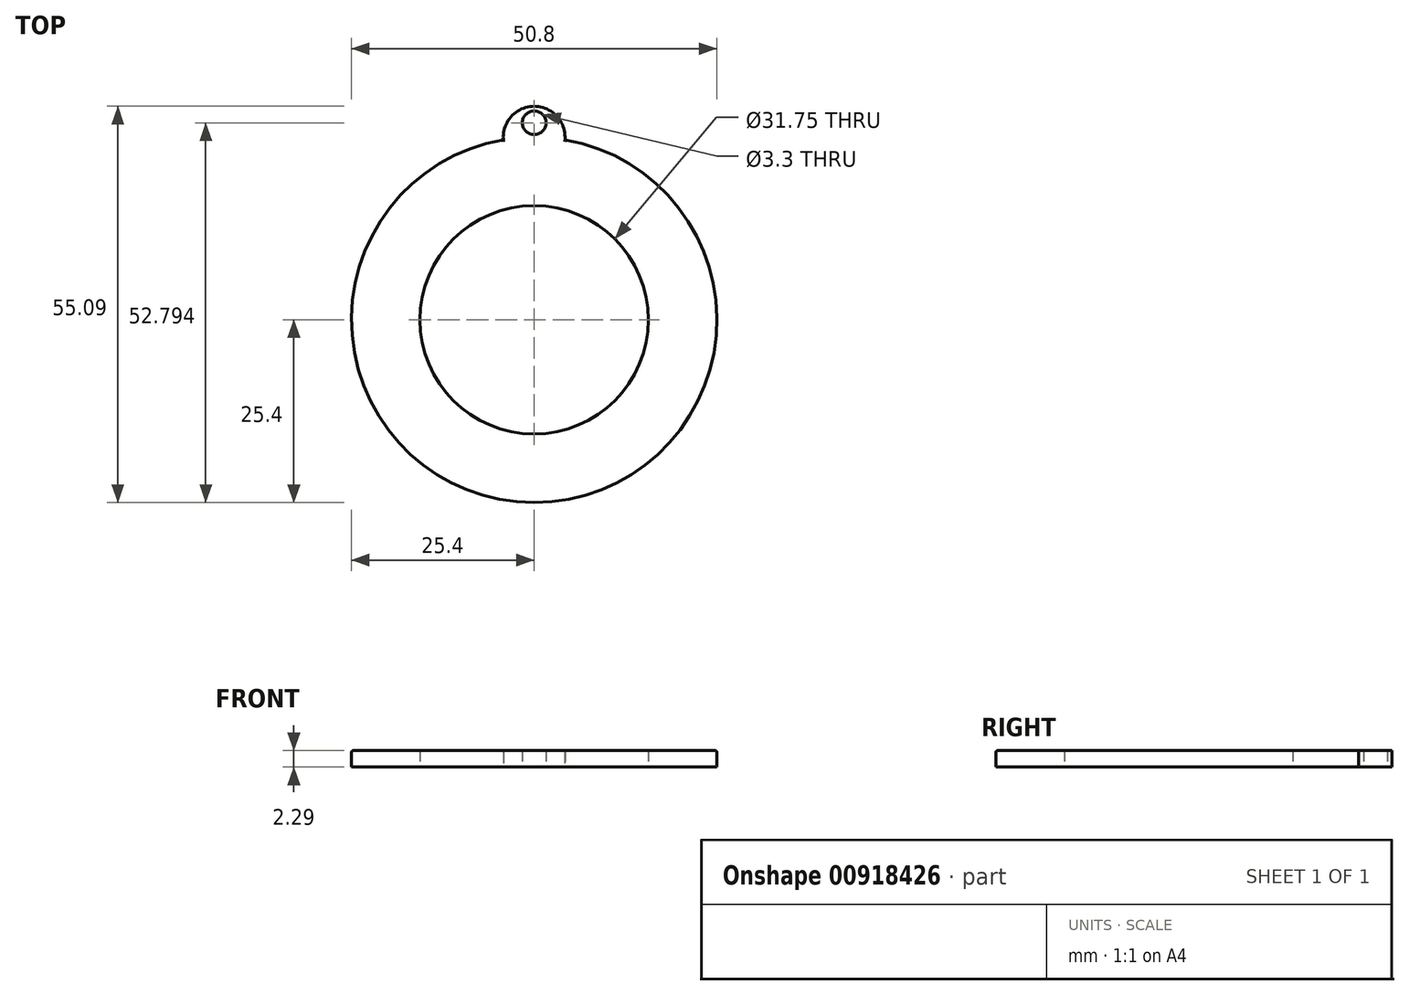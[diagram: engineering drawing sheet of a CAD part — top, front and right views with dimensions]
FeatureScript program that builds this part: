
annotation { "Feature Type Name" : "Feature", "Feature Type Description" : "" }
export const myFeature = defineFeature(function(context is Context, id is Id, definition is map)
    precondition{}
    {
        {
            var Q0;
            Q0=qCreatedBy(makeId("Top.planeOp"),FACE);
            var sketch = newSketch(context, id + "F0", { "sketchPlane" : qUnion([Q0])});
            skArc(sketch, "E0", {"start": v(-5.16, 24.87) * mm, "mid": v(0, -25.4) * mm, "end": v(5.16, 24.87) * mm});
            skPoint(sketch, "E1.center.orphan", {"position": v(0, 28.38) * mm});
            skPoint(sketch, "E2.visualSharp", {"position": v(-3.17, 25.2) * mm});
            skPoint(sketch, "E3.visualSharp", {"position": v(3.17, 25.2) * mm});
            skCircle(sketch, "E4", {"center": v(0, 0) * mm, "radius": 15.88 * mm});
            skArc(sketch, "E5", {"start": v(4.29, 25.19) * mm, "mid": v(0, 29.7) * mm, "end": v(-4.29, 25.19) * mm});
            skCircle(sketch, "E6", {"center": v(0, 27.4) * mm, "radius": 1.65 * mm});
            skPoint(sketch, "E7.center.orphan", {"position": v(0, 26.55) * mm});
            skArc(sketch, "E8", {"start": v(-5.16, 24.87) * mm, "mid": v(-4.72, 24.96) * mm, "end": v(-4.28, 25.04) * mm});
            skArc(sketch, "E9", {"start": v(4.29, 25.19) * mm, "mid": v(4.28, 25.11) * mm, "end": v(4.28, 25.04) * mm});
            skArc(sketch, "E10.trimOffspring", {"start": v(4.28, 25.04) * mm, "mid": v(4.72, 24.96) * mm, "end": v(5.16, 24.87) * mm});
            skArc(sketch, "E11.trimOffspring", {"start": v(-4.28, 25.04) * mm, "mid": v(-4.28, 25.11) * mm, "end": v(-4.29, 25.19) * mm});
            skSolve(sketch);
        }
        {
            var Q0;
            Q0=makeQuery(id+"F0.imprint","IMPRINT",FACE,{"disambiguationData":[TD([[makeQuery(id+"F0.imprint","IMPRINT",EDGE,{"derivedFrom":sQuery(id+"F0.wireOp",EDGE,"E0")}),1.0]])]});
            extrude(context, id + "F1", {"entities" : qUnion([Q0]), "depth" : 2.3 * mm, "offsetDistance" : 25.4 * mm});
        }
        {
            var Q0;
            Q0=makeQuery(id+"F1.opExtrude","CAP_EDGE",EDGE,{"disambiguationData":[OSD([sQuery(id+"F0.wireOp",EDGE,"E0")])],"isStart":false});
            var Q1;
            Q1=makeQuery(id+"F1.opExtrude","CAP_EDGE",EDGE,{"disambiguationData":[OSD([sQuery(id+"F0.wireOp",EDGE,"E3.filletArc")])],"isStart":false});
            var Q2;
            Q2=makeQuery(id+"F1.opExtrude","CAP_EDGE",EDGE,{"disambiguationData":[OSD([sQuery(id+"F0.wireOp",EDGE,"fad7691f-57ae-4f9e-b21f-8166f6ef767e.trimOffspring")])],"isStart":false});
            var Q3;
            Q3=makeQuery(id+"F1.opExtrude","CAP_EDGE",EDGE,{"disambiguationData":[OSD([sQuery(id+"F0.wireOp",EDGE,"AylRhy1O-DjiZ-3hJw-jLin-TCy3Srt4XLs0")])],"isStart":false});
            var Q4;
            Q4=makeQuery(id+"F1.opExtrude","CAP_EDGE",EDGE,{"disambiguationData":[OSD([sQuery(id+"F0.wireOp",EDGE,"E2.filletArc")])],"isStart":false});
            var Q5;
            Q5=makeQuery(id+"F1.opExtrude","CAP_EDGE",EDGE,{"disambiguationData":[OSD([sQuery(id+"F0.wireOp",EDGE,"lUi0VhGP-HKFJ-G4Bn-hLa6-QLbGJ3k8ofbs")])],"isStart":false});
            var Q6;
            Q6=makeQuery(id+"F1.opExtrude","CAP_EDGE",EDGE,{"disambiguationData":[OSD([sQuery(id+"F0.wireOp",EDGE,"E7"),sQuery(id+"F0.wireOp",EDGE,"f33125d6-0fcc-48fc-a28e-0dbd31db5ab6.trimOffspring"),sQuery(id+"F0.wireOp",EDGE,"37a20bed-02d5-4644-b29c-c1de4f5cb0e1")])],"isStart":false});
            var Q7;
            Q7=makeQuery(id+"F1.opExtrude","CAP_EDGE",EDGE,{"disambiguationData":[OSD([sQuery(id+"F0.wireOp",EDGE,"fNGFwmxS-K0MY-4eJI-Mism-aGGH0b7Q9qfj")])],"isStart":false});
            fillet(context, id + "F2", {"entities" : qUnion([Q0, Q1, Q2, Q3, Q4, Q5, Q6, Q7]), "radius" : 0.25 * mm, "tangentPropagation" : true, "allowEdgeOverflow" : false});
        }
    });
